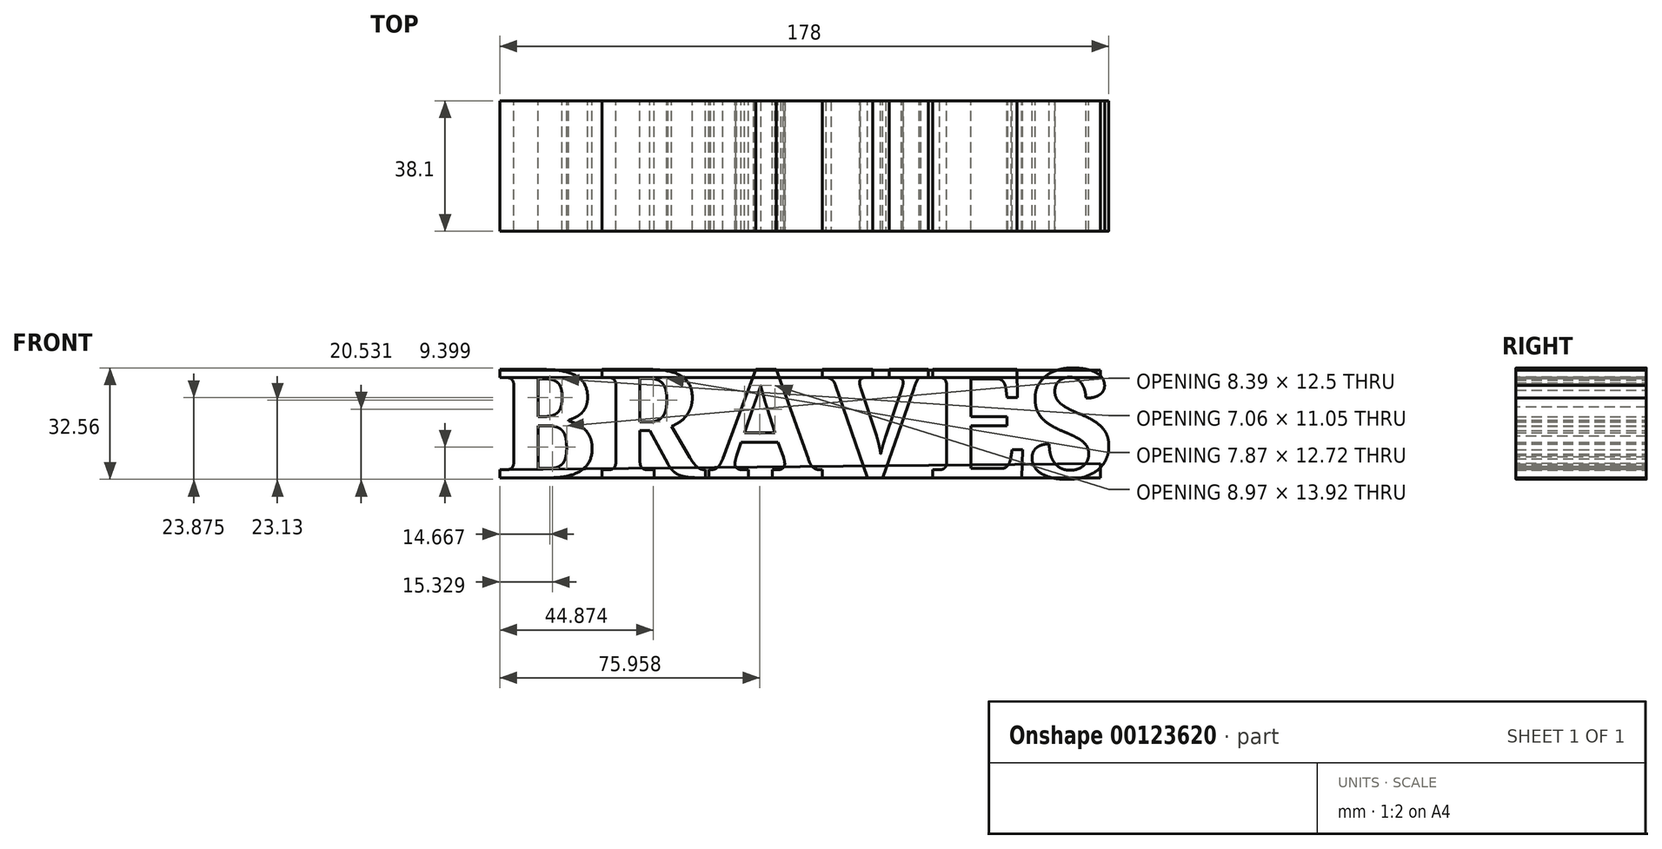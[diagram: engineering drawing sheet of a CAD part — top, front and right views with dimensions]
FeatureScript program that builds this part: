
annotation { "Feature Type Name" : "Feature", "Feature Type Description" : "" }
export const myFeature = defineFeature(function(context is Context, id is Id, definition is map)
    precondition{}
    {
        {
            var Q0;
            Q0=qCreatedBy(makeId("Front.planeOp"),FACE);
            var sketch = newSketch(context, id + "F0", { "sketchPlane" : qUnion([Q0])});
            skText(sketch, "E0", { "text": "BRAVES", "fontName": "NotoSerif-Bold.ttf"});
            const initialGuessF0  = {"E0": [-0.08006, 0, 1, 0, 0.03194]};
            skSetInitialGuess(sketch, initialGuessF0);
            skSolve(sketch);
        }
        {
            var Q0;
            Q0 = qSketchRegion(id + "F0", true);
            extrude(context, id + "F1", {"entities" : qUnion([Q0]), "depth" : 38.1 * mm});
        }
        {
            var Q0;
            Q0=makeQuery(id+"F1.opExtrude","CAP_FACE",FACE,{"disambiguationData":[OSD([sQuery(id+"F0.wireOp",EDGE,"E0.sketch_text.stroke-0"),sQuery(id+"F0.wireOp",EDGE,"E0.sketch_text.stroke-1"),sQuery(id+"F0.wireOp",EDGE,"E0.sketch_text.stroke-2"),sQuery(id+"F0.wireOp",EDGE,"E0.sketch_text.stroke-3"),sQuery(id+"F0.wireOp",EDGE,"E0.sketch_text.stroke-4"),sQuery(id+"F0.wireOp",EDGE,"E0.sketch_text.stroke-5"),sQuery(id+"F0.wireOp",EDGE,"E0.sketch_text.stroke-6"),sQuery(id+"F0.wireOp",EDGE,"E0.sketch_text.stroke-7"),sQuery(id+"F0.wireOp",EDGE,"E0.sketch_text.stroke-8"),sQuery(id+"F0.wireOp",EDGE,"E0.sketch_text.stroke-9"),sQuery(id+"F0.wireOp",EDGE,"E0.sketch_text.stroke-10"),sQuery(id+"F0.wireOp",EDGE,"E0.sketch_text.stroke-11"),sQuery(id+"F0.wireOp",EDGE,"E0.sketch_text.stroke-12"),sQuery(id+"F0.wireOp",EDGE,"E0.sketch_text.stroke-13"),sQuery(id+"F0.wireOp",EDGE,"E0.sketch_text.stroke-14"),sQuery(id+"F0.wireOp",EDGE,"E0.sketch_text.stroke-15"),sQuery(id+"F0.wireOp",EDGE,"E0.sketch_text.stroke-16"),sQuery(id+"F0.wireOp",EDGE,"E0.sketch_text.stroke-17"),sQuery(id+"F0.wireOp",EDGE,"E0.sketch_text.stroke-18"),sQuery(id+"F0.wireOp",EDGE,"E0.sketch_text.stroke-19"),sQuery(id+"F0.wireOp",EDGE,"E0.sketch_text.stroke-20"),sQuery(id+"F0.wireOp",EDGE,"E0.sketch_text.stroke-21"),sQuery(id+"F0.wireOp",EDGE,"E0.sketch_text.stroke-22"),sQuery(id+"F0.wireOp",EDGE,"E0.sketch_text.stroke-23"),sQuery(id+"F0.wireOp",EDGE,"E0.sketch_text.stroke-24"),sQuery(id+"F0.wireOp",EDGE,"E0.sketch_text.stroke-25"),sQuery(id+"F0.wireOp",EDGE,"E0.sketch_text.stroke-26"),sQuery(id+"F0.wireOp",EDGE,"E0.sketch_text.stroke-27"),sQuery(id+"F0.wireOp",EDGE,"E0.sketch_text.stroke-28"),sQuery(id+"F0.wireOp",EDGE,"E0.sketch_text.stroke-29"),sQuery(id+"F0.wireOp",EDGE,"E0.sketch_text.stroke-30"),sQuery(id+"F0.wireOp",EDGE,"E0.sketch_text.stroke-31"),sQuery(id+"F0.wireOp",EDGE,"E0.sketch_text.stroke-32"),sQuery(id+"F0.wireOp",EDGE,"E0.sketch_text.stroke-33"),sQuery(id+"F0.wireOp",EDGE,"E0.sketch_text.stroke-34"),sQuery(id+"F0.wireOp",EDGE,"E0.sketch_text.stroke-35"),sQuery(id+"F0.wireOp",EDGE,"E0.sketch_text.stroke-36"),sQuery(id+"F0.wireOp",EDGE,"E0.sketch_text.stroke-37"),sQuery(id+"F0.wireOp",EDGE,"E0.sketch_text.stroke-38"),sQuery(id+"F0.wireOp",EDGE,"E0.sketch_text.stroke-39"),sQuery(id+"F0.wireOp",EDGE,"E0.sketch_text.stroke-40"),sQuery(id+"F0.wireOp",EDGE,"E0.sketch_text.stroke-41"),sQuery(id+"F0.wireOp",EDGE,"E0.sketch_text.stroke-42"),sQuery(id+"F0.wireOp",EDGE,"E0.sketch_text.stroke-43"),sQuery(id+"F0.wireOp",EDGE,"E0.sketch_text.stroke-44"),sQuery(id+"F0.wireOp",EDGE,"E0.sketch_text.stroke-45"),sQuery(id+"F0.wireOp",EDGE,"E0.sketch_text.stroke-46"),sQuery(id+"F0.wireOp",EDGE,"E0.sketch_text.stroke-47"),sQuery(id+"F0.wireOp",EDGE,"E0.sketch_text.stroke-48"),sQuery(id+"F0.wireOp",EDGE,"E0.sketch_text.stroke-49")])],"isStart":false});
            var sketch = newSketch(context, id + "F2", { "sketchPlane" : qUnion([Q0])});
            skLineSegment(sketch, "E1", {"start": v(-78.83, 2.36) * mm, "end": v(96.7, 4.12) * mm});
            skLineSegment(sketch, "E2", {"start": v(96.7, 4.12) * mm, "end": v(96.74, 0) * mm});
            skLineSegment(sketch, "E3", {"start": v(96.74, 0) * mm, "end": v(-78.83, 0) * mm});
            skLineSegment(sketch, "E4", {"start": v(-78.83, 0) * mm, "end": v(-78.83, 2.36) * mm});
            skSolve(sketch);
        }
        {
            var Q0;
            Q0 = qSketchRegion(id + "F2", true);
            extrude(context, id + "F3", {"entities" : qUnion([Q0]), "oppositeDirection" : true, "depth" : 38.1 * mm});
        }
        {
            var Q0;
            Q0=qCreatedBy(makeId("Front.planeOp"),FACE);
            var sketch = newSketch(context, id + "F4", { "sketchPlane" : qUnion([Q0])});
            skLineSegment(sketch, "E5", {"start": v(-78.8, 29.32) * mm, "end": v(96.72, 29.32) * mm});
            skLineSegment(sketch, "E6", {"start": v(96.72, 29.32) * mm, "end": v(96.72, 31.52) * mm});
            skLineSegment(sketch, "E7", {"start": v(96.72, 31.52) * mm, "end": v(-78.82, 31.52) * mm});
            skLineSegment(sketch, "E8", {"start": v(-78.82, 31.52) * mm, "end": v(-78.8, 29.32) * mm});
            skSolve(sketch);
        }
        {
            var Q0;
            Q0 = qSketchRegion(id + "F4", true);
            extrude(context, id + "F5", {"entities" : qUnion([Q0]), "depth" : 38.1 * mm});
        }
    });
